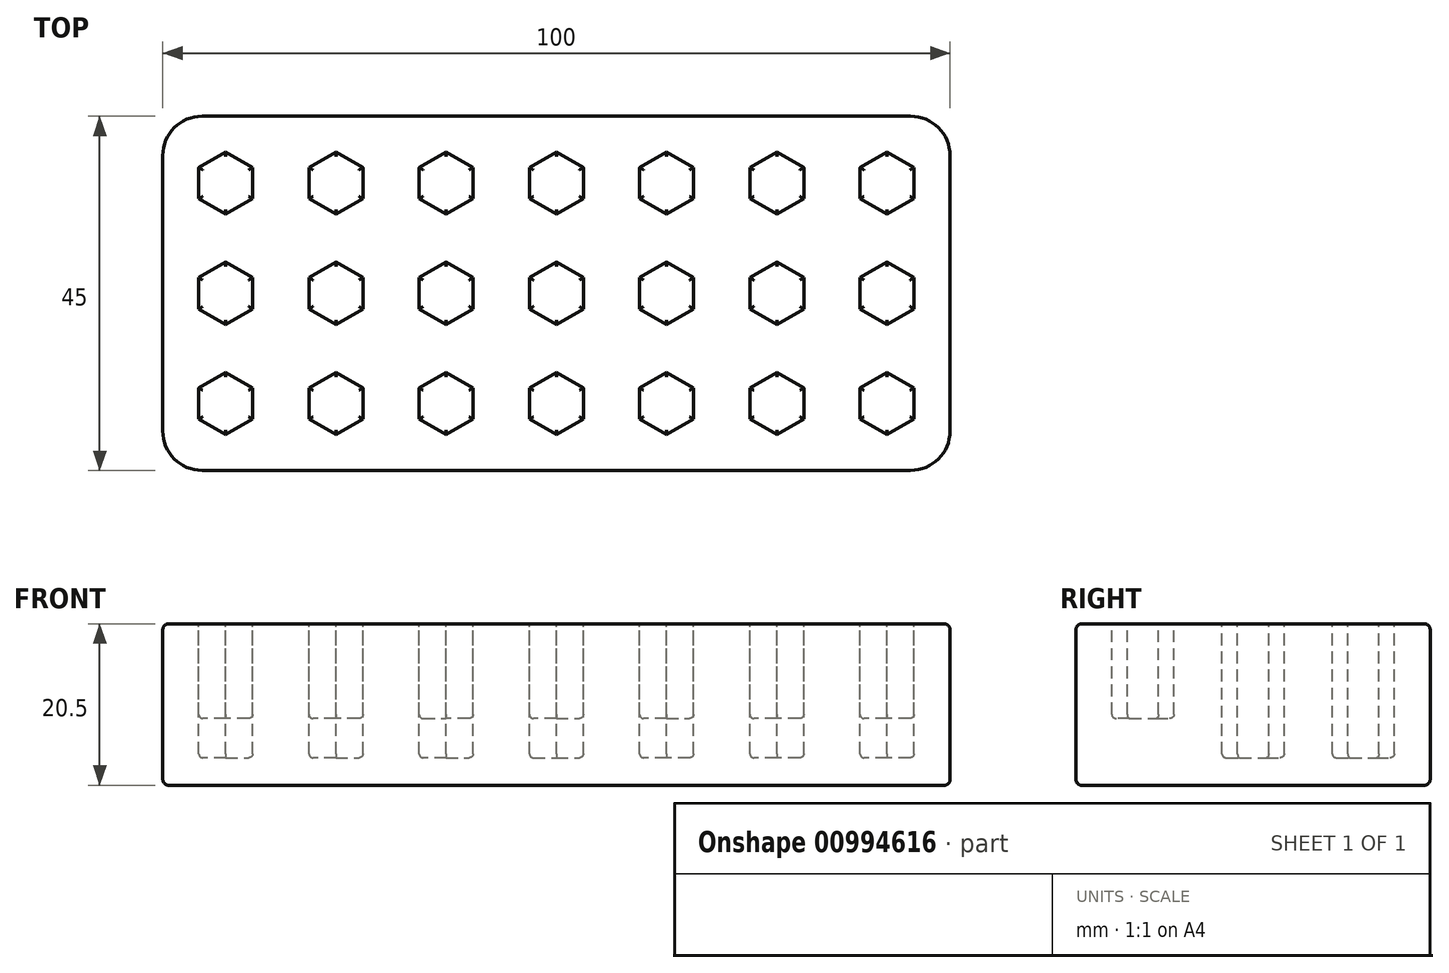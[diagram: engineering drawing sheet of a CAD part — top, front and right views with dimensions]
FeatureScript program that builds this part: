
annotation { "Feature Type Name" : "Feature", "Feature Type Description" : "" }
export const myFeature = defineFeature(function(context is Context, id is Id, definition is map)
    precondition{}
    {
        {
            var Q0;
            Q0=qCreatedBy(makeId("Top.planeOp"),FACE);
            var sketch = newSketch(context, id + "F0", { "sketchPlane" : qUnion([Q0])});
            skLineSegment(sketch, "E0.bottom", {"start": v(45, -22.5) * mm, "end": v(-45, -22.5) * mm});
            skLineSegment(sketch, "E0.top", {"start": v(45, 22.5) * mm, "end": v(-45, 22.5) * mm});
            skLineSegment(sketch, "E0.left", {"start": v(50, -17.5) * mm, "end": v(50, 17.5) * mm});
            skLineSegment(sketch, "E0.right", {"start": v(-50, -17.5) * mm, "end": v(-50, 17.5) * mm});
            skPoint(sketch, "E0.middle", {"position": v(0, 0) * mm});
            skPoint(sketch, "E1.visualSharp", {"position": v(-50, 22.5) * mm});
            skArc(sketch, "E1.filletArc", {"start": v(-45, 22.5) * mm, "mid": v(-48.54, 21.04) * mm, "end": v(-50, 17.5) * mm});
            skPoint(sketch, "E2.visualSharp", {"position": v(50, 22.5) * mm});
            skArc(sketch, "E2.filletArc", {"start": v(50, 17.5) * mm, "mid": v(48.54, 21.04) * mm, "end": v(45, 22.5) * mm});
            skPoint(sketch, "E3.visualSharp", {"position": v(50, -22.5) * mm});
            skArc(sketch, "E3.filletArc", {"start": v(45, -22.5) * mm, "mid": v(48.54, -21.04) * mm, "end": v(50, -17.5) * mm});
            skPoint(sketch, "E4.visualSharp", {"position": v(-50, -22.5) * mm});
            skArc(sketch, "E4.filletArc", {"start": v(-50, -17.5) * mm, "mid": v(-48.54, -21.04) * mm, "end": v(-45, -22.5) * mm});
            skCircle(sketch, "E5.cCircle", {"center": v(0, 0) * mm, "radius": 3.43 * mm, "construction": true});
            skLineSegment(sketch, "E5.0", {"start": v(3.43, 1.98) * mm, "end": v(3.43, -1.98) * mm});
            skLineSegment(sketch, "E5.1", {"start": v(3.43, -1.98) * mm, "end": v(0, -3.95) * mm});
            skLineSegment(sketch, "E5.2", {"start": v(0, -3.95) * mm, "end": v(-3.43, -1.98) * mm});
            skLineSegment(sketch, "E5.3", {"start": v(-3.43, -1.98) * mm, "end": v(-3.43, 1.98) * mm});
            skLineSegment(sketch, "E5.4", {"start": v(-3.43, 1.98) * mm, "end": v(0, 3.95) * mm});
            skLineSegment(sketch, "E5.5", {"start": v(0, 3.95) * mm, "end": v(3.43, 1.98) * mm});
            skPoint(sketch, "E5.0.midPoint", {"position": v(3.43, 0) * mm});
            skLineSegment(sketch, "E6.0.1.0", {"start": v(-3.43, 15.98) * mm, "end": v(0, 17.95) * mm});
            skLineSegment(sketch, "E6.0.1.1", {"start": v(3.43, 12.02) * mm, "end": v(0, 10.05) * mm});
            skLineSegment(sketch, "E6.0.1.2", {"start": v(3.43, 15.98) * mm, "end": v(3.43, 12.02) * mm});
            skPoint(sketch, "E6.0.1.3", {"position": v(3.43, 14) * mm});
            skLineSegment(sketch, "E6.0.1.4", {"start": v(0, 10.05) * mm, "end": v(-3.43, 12.02) * mm});
            skLineSegment(sketch, "E6.0.1.5", {"start": v(-3.43, 12.02) * mm, "end": v(-3.43, 15.98) * mm});
            skCircle(sketch, "E6.0.1.6", {"center": v(0, 14) * mm, "radius": 3.43 * mm, "construction": true});
            skLineSegment(sketch, "E6.0.1.7", {"start": v(0, 17.95) * mm, "end": v(3.43, 15.98) * mm});
            skPoint(sketch, "E6.0.1.8", {"position": v(0, 14) * mm});
            skLineSegment(sketch, "E6.1.0.0", {"start": v(10.58, 1.98) * mm, "end": v(14, 3.95) * mm});
            skLineSegment(sketch, "E6.1.0.1", {"start": v(17.43, -1.98) * mm, "end": v(14, -3.95) * mm});
            skLineSegment(sketch, "E6.1.0.2", {"start": v(17.43, 1.98) * mm, "end": v(17.43, -1.98) * mm});
            skPoint(sketch, "E6.1.0.3", {"position": v(17.43, 0) * mm});
            skLineSegment(sketch, "E6.1.0.4", {"start": v(14, -3.95) * mm, "end": v(10.58, -1.98) * mm});
            skLineSegment(sketch, "E6.1.0.5", {"start": v(10.58, -1.98) * mm, "end": v(10.58, 1.98) * mm});
            skCircle(sketch, "E6.1.0.6", {"center": v(14, 0) * mm, "radius": 3.43 * mm, "construction": true});
            skLineSegment(sketch, "E6.1.0.7", {"start": v(14, 3.95) * mm, "end": v(17.43, 1.98) * mm});
            skPoint(sketch, "E6.1.0.8", {"position": v(14, 0) * mm});
            skLineSegment(sketch, "E6.1.1.0", {"start": v(10.58, 15.98) * mm, "end": v(14, 17.95) * mm});
            skLineSegment(sketch, "E6.1.1.1", {"start": v(17.43, 12.02) * mm, "end": v(14, 10.05) * mm});
            skLineSegment(sketch, "E6.1.1.2", {"start": v(17.43, 15.98) * mm, "end": v(17.43, 12.02) * mm});
            skPoint(sketch, "E6.1.1.3", {"position": v(17.43, 14) * mm});
            skLineSegment(sketch, "E6.1.1.4", {"start": v(14, 10.05) * mm, "end": v(10.58, 12.02) * mm});
            skLineSegment(sketch, "E6.1.1.5", {"start": v(10.58, 12.02) * mm, "end": v(10.58, 15.98) * mm});
            skCircle(sketch, "E6.1.1.6", {"center": v(14, 14) * mm, "radius": 3.43 * mm, "construction": true});
            skLineSegment(sketch, "E6.1.1.7", {"start": v(14, 17.95) * mm, "end": v(17.43, 15.98) * mm});
            skPoint(sketch, "E6.1.1.8", {"position": v(14, 14) * mm});
            skLineSegment(sketch, "E6.2.0.0", {"start": v(24.58, 1.98) * mm, "end": v(28, 3.95) * mm});
            skLineSegment(sketch, "E6.2.0.1", {"start": v(31.43, -1.98) * mm, "end": v(28, -3.95) * mm});
            skLineSegment(sketch, "E6.2.0.2", {"start": v(31.43, 1.98) * mm, "end": v(31.43, -1.98) * mm});
            skPoint(sketch, "E6.2.0.3", {"position": v(31.43, 0) * mm});
            skLineSegment(sketch, "E6.2.0.4", {"start": v(28, -3.95) * mm, "end": v(24.58, -1.98) * mm});
            skLineSegment(sketch, "E6.2.0.5", {"start": v(24.58, -1.98) * mm, "end": v(24.58, 1.98) * mm});
            skCircle(sketch, "E6.2.0.6", {"center": v(28, 0) * mm, "radius": 3.43 * mm, "construction": true});
            skLineSegment(sketch, "E6.2.0.7", {"start": v(28, 3.95) * mm, "end": v(31.43, 1.98) * mm});
            skPoint(sketch, "E6.2.0.8", {"position": v(28, 0) * mm});
            skLineSegment(sketch, "E6.2.1.0", {"start": v(24.58, 15.98) * mm, "end": v(28, 17.95) * mm});
            skLineSegment(sketch, "E6.2.1.1", {"start": v(31.43, 12.02) * mm, "end": v(28, 10.05) * mm});
            skLineSegment(sketch, "E6.2.1.2", {"start": v(31.43, 15.98) * mm, "end": v(31.43, 12.02) * mm});
            skPoint(sketch, "E6.2.1.3", {"position": v(31.43, 14) * mm});
            skLineSegment(sketch, "E6.2.1.4", {"start": v(28, 10.05) * mm, "end": v(24.58, 12.02) * mm});
            skLineSegment(sketch, "E6.2.1.5", {"start": v(24.58, 12.02) * mm, "end": v(24.58, 15.98) * mm});
            skCircle(sketch, "E6.2.1.6", {"center": v(28, 14) * mm, "radius": 3.43 * mm, "construction": true});
            skLineSegment(sketch, "E6.2.1.7", {"start": v(28, 17.95) * mm, "end": v(31.43, 15.98) * mm});
            skPoint(sketch, "E6.2.1.8", {"position": v(28, 14) * mm});
            skLineSegment(sketch, "E6.3.0.0", {"start": v(38.58, 1.98) * mm, "end": v(42, 3.95) * mm});
            skLineSegment(sketch, "E6.3.0.1", {"start": v(45.43, -1.98) * mm, "end": v(42, -3.95) * mm});
            skLineSegment(sketch, "E6.3.0.2", {"start": v(45.43, 1.98) * mm, "end": v(45.43, -1.98) * mm});
            skPoint(sketch, "E6.3.0.3", {"position": v(45.43, 0) * mm});
            skLineSegment(sketch, "E6.3.0.4", {"start": v(42, -3.95) * mm, "end": v(38.58, -1.98) * mm});
            skLineSegment(sketch, "E6.3.0.5", {"start": v(38.58, -1.98) * mm, "end": v(38.58, 1.98) * mm});
            skCircle(sketch, "E6.3.0.6", {"center": v(42, 0) * mm, "radius": 3.43 * mm, "construction": true});
            skLineSegment(sketch, "E6.3.0.7", {"start": v(42, 3.95) * mm, "end": v(45.43, 1.98) * mm});
            skPoint(sketch, "E6.3.0.8", {"position": v(42, 0) * mm});
            skLineSegment(sketch, "E6.3.1.0", {"start": v(38.58, 15.98) * mm, "end": v(42, 17.95) * mm});
            skLineSegment(sketch, "E6.3.1.1", {"start": v(45.43, 12.02) * mm, "end": v(42, 10.05) * mm});
            skLineSegment(sketch, "E6.3.1.2", {"start": v(45.43, 15.98) * mm, "end": v(45.43, 12.02) * mm});
            skPoint(sketch, "E6.3.1.3", {"position": v(45.43, 14) * mm});
            skLineSegment(sketch, "E6.3.1.4", {"start": v(42, 10.05) * mm, "end": v(38.58, 12.02) * mm});
            skLineSegment(sketch, "E6.3.1.5", {"start": v(38.58, 12.02) * mm, "end": v(38.58, 15.98) * mm});
            skCircle(sketch, "E6.3.1.6", {"center": v(42, 14) * mm, "radius": 3.43 * mm, "construction": true});
            skLineSegment(sketch, "E6.3.1.7", {"start": v(42, 17.95) * mm, "end": v(45.43, 15.98) * mm});
            skPoint(sketch, "E6.3.1.8", {"position": v(42, 14) * mm});
            skLineSegment(sketch, "E6.direction1", {"start": v(-3.43, -1.98) * mm, "end": v(10.58, -1.98) * mm, "construction": true});
            skLineSegment(sketch, "E6.direction2", {"start": v(-3.43, -1.98) * mm, "end": v(-3.43, 12.02) * mm, "construction": true});
            skLineSegment(sketch, "E7", {"start": v(0, 36.48) * mm, "end": v(0, -38.23) * mm, "construction": true});
            skLineSegment(sketch, "E8.MirrorCS", {"start": v(-10.58, 15.98) * mm, "end": v(-14, 17.95) * mm});
            skLineSegment(sketch, "E9.MirrorCS", {"start": v(-14, 17.95) * mm, "end": v(-17.43, 15.98) * mm});
            skLineSegment(sketch, "E10.MirrorCS", {"start": v(-17.43, 15.98) * mm, "end": v(-17.43, 12.02) * mm});
            skLineSegment(sketch, "E11.MirrorCS", {"start": v(-17.43, 12.02) * mm, "end": v(-14, 10.05) * mm});
            skLineSegment(sketch, "E12.MirrorCS", {"start": v(-14, 10.05) * mm, "end": v(-10.58, 12.02) * mm});
            skLineSegment(sketch, "E13.MirrorCS", {"start": v(-10.58, 12.02) * mm, "end": v(-10.58, 15.98) * mm});
            skLineSegment(sketch, "E14.MirrorCS", {"start": v(-24.58, 12.02) * mm, "end": v(-24.58, 15.98) * mm});
            skLineSegment(sketch, "E15.MirrorCS", {"start": v(-24.58, 15.98) * mm, "end": v(-28, 17.95) * mm});
            skLineSegment(sketch, "E16.MirrorCS", {"start": v(-28, 17.95) * mm, "end": v(-31.43, 15.98) * mm});
            skLineSegment(sketch, "E17.MirrorCS", {"start": v(-31.43, 15.98) * mm, "end": v(-31.43, 12.02) * mm});
            skLineSegment(sketch, "E18.MirrorCS", {"start": v(-31.43, 12.02) * mm, "end": v(-28, 10.05) * mm});
            skLineSegment(sketch, "E19.MirrorCS", {"start": v(-28, 3.95) * mm, "end": v(-31.43, 1.98) * mm});
            skLineSegment(sketch, "E20.MirrorCS", {"start": v(-24.58, 1.98) * mm, "end": v(-28, 3.95) * mm});
            skLineSegment(sketch, "E21.MirrorCS", {"start": v(-24.58, -1.98) * mm, "end": v(-24.58, 1.98) * mm});
            skLineSegment(sketch, "E22.MirrorCS", {"start": v(-28, -3.95) * mm, "end": v(-24.58, -1.98) * mm});
            skLineSegment(sketch, "E23.MirrorCS", {"start": v(-31.43, -1.98) * mm, "end": v(-28, -3.95) * mm});
            skLineSegment(sketch, "E24.MirrorCS", {"start": v(-28, 10.05) * mm, "end": v(-24.58, 12.02) * mm});
            skLineSegment(sketch, "E25.MirrorCS", {"start": v(-31.43, 1.98) * mm, "end": v(-31.43, -1.98) * mm});
            skLineSegment(sketch, "E26.MirrorCS", {"start": v(-38.58, 15.98) * mm, "end": v(-42, 17.95) * mm});
            skLineSegment(sketch, "E27.MirrorCS", {"start": v(-42, 17.95) * mm, "end": v(-45.43, 15.98) * mm});
            skLineSegment(sketch, "E28.MirrorCS", {"start": v(-45.43, 15.98) * mm, "end": v(-45.43, 12.02) * mm});
            skLineSegment(sketch, "E29.MirrorCS", {"start": v(-45.43, 12.02) * mm, "end": v(-42, 10.05) * mm});
            skLineSegment(sketch, "E30.MirrorCS", {"start": v(-42, 10.05) * mm, "end": v(-38.58, 12.02) * mm});
            skLineSegment(sketch, "E31.MirrorCS", {"start": v(-38.58, 12.02) * mm, "end": v(-38.58, 15.98) * mm});
            skLineSegment(sketch, "E32.MirrorCS", {"start": v(-38.58, 1.98) * mm, "end": v(-42, 3.95) * mm});
            skLineSegment(sketch, "E33.MirrorCS", {"start": v(-42, 3.95) * mm, "end": v(-45.43, 1.98) * mm});
            skLineSegment(sketch, "E34.MirrorCS", {"start": v(-45.43, 1.98) * mm, "end": v(-45.43, -1.98) * mm});
            skLineSegment(sketch, "E35.MirrorCS", {"start": v(-45.43, -1.98) * mm, "end": v(-42, -3.95) * mm});
            skLineSegment(sketch, "E36.MirrorCS", {"start": v(-42, -3.95) * mm, "end": v(-38.58, -1.98) * mm});
            skLineSegment(sketch, "E37.MirrorCS", {"start": v(-38.58, -1.98) * mm, "end": v(-38.58, 1.98) * mm});
            skLineSegment(sketch, "E38.MirrorCS", {"start": v(-10.58, 1.98) * mm, "end": v(-14, 3.95) * mm});
            skLineSegment(sketch, "E39.MirrorCS", {"start": v(-14, 3.95) * mm, "end": v(-17.43, 1.98) * mm});
            skLineSegment(sketch, "E40.MirrorCS", {"start": v(-17.43, 1.98) * mm, "end": v(-17.43, -1.98) * mm});
            skLineSegment(sketch, "E41.MirrorCS", {"start": v(-17.43, -1.98) * mm, "end": v(-14, -3.95) * mm});
            skLineSegment(sketch, "E42.MirrorCS", {"start": v(-14, -3.95) * mm, "end": v(-10.58, -1.98) * mm});
            skLineSegment(sketch, "E43.MirrorCS", {"start": v(-10.58, -1.98) * mm, "end": v(-10.58, 1.98) * mm});
            skLineSegment(sketch, "E44", {"start": v(-62.75, 0) * mm, "end": v(58.2, 0) * mm, "construction": true});
            skLineSegment(sketch, "E45.MirrorCS", {"start": v(-31.43, -12.02) * mm, "end": v(-28, -10.05) * mm});
            skLineSegment(sketch, "E46.MirrorCS", {"start": v(-45.43, -12.02) * mm, "end": v(-42, -10.05) * mm});
            skLineSegment(sketch, "E47.MirrorCS", {"start": v(-28, -17.95) * mm, "end": v(-31.43, -15.98) * mm});
            skLineSegment(sketch, "E48.MirrorCS", {"start": v(-10.58, -15.98) * mm, "end": v(-14, -17.95) * mm});
            skLineSegment(sketch, "E49.MirrorCS", {"start": v(-38.58, -12.02) * mm, "end": v(-38.58, -15.98) * mm});
            skLineSegment(sketch, "E50.MirrorCS", {"start": v(-42, -10.05) * mm, "end": v(-38.58, -12.02) * mm});
            skLineSegment(sketch, "E51.MirrorCS", {"start": v(-31.43, -15.98) * mm, "end": v(-31.43, -12.02) * mm});
            skLineSegment(sketch, "E52.MirrorCS", {"start": v(-45.43, -15.98) * mm, "end": v(-45.43, -12.02) * mm});
            skLineSegment(sketch, "E53.MirrorCS", {"start": v(-24.58, -15.98) * mm, "end": v(-28, -17.95) * mm});
            skLineSegment(sketch, "E54.MirrorCS", {"start": v(-38.58, -15.98) * mm, "end": v(-42, -17.95) * mm});
            skLineSegment(sketch, "E55.MirrorCS", {"start": v(-14, -10.05) * mm, "end": v(-10.58, -12.02) * mm});
            skLineSegment(sketch, "E56.MirrorCS", {"start": v(-10.58, -12.02) * mm, "end": v(-10.58, -15.98) * mm});
            skLineSegment(sketch, "E57.MirrorCS", {"start": v(-28, -10.05) * mm, "end": v(-24.58, -12.02) * mm});
            skLineSegment(sketch, "E58.MirrorCS", {"start": v(-17.43, -12.02) * mm, "end": v(-14, -10.05) * mm});
            skLineSegment(sketch, "E59.MirrorCS", {"start": v(-17.43, -15.98) * mm, "end": v(-17.43, -12.02) * mm});
            skLineSegment(sketch, "E60.MirrorCS", {"start": v(-14, -17.95) * mm, "end": v(-17.43, -15.98) * mm});
            skLineSegment(sketch, "E61.MirrorCS", {"start": v(-42, -17.95) * mm, "end": v(-45.43, -15.98) * mm});
            skLineSegment(sketch, "E62.MirrorCS", {"start": v(-24.58, -12.02) * mm, "end": v(-24.58, -15.98) * mm});
            skLineSegment(sketch, "E63.MirrorCS", {"start": v(-3.43, -15.98) * mm, "end": v(0, -17.95) * mm});
            skLineSegment(sketch, "E64.MirrorCS", {"start": v(0, -17.95) * mm, "end": v(3.43, -15.98) * mm});
            skLineSegment(sketch, "E65.MirrorCS", {"start": v(3.43, -15.98) * mm, "end": v(3.43, -12.02) * mm});
            skLineSegment(sketch, "E66.MirrorCS", {"start": v(3.43, -12.02) * mm, "end": v(0, -10.05) * mm});
            skLineSegment(sketch, "E67.MirrorCS", {"start": v(0, -10.05) * mm, "end": v(-3.43, -12.02) * mm});
            skLineSegment(sketch, "E68.MirrorCS", {"start": v(-3.43, -12.02) * mm, "end": v(-3.43, -15.98) * mm});
            skLineSegment(sketch, "E69.MirrorCS", {"start": v(10.58, -15.98) * mm, "end": v(14, -17.95) * mm});
            skLineSegment(sketch, "E70.MirrorCS", {"start": v(14, -17.95) * mm, "end": v(17.43, -15.98) * mm});
            skLineSegment(sketch, "E71.MirrorCS", {"start": v(17.43, -15.98) * mm, "end": v(17.43, -12.02) * mm});
            skLineSegment(sketch, "E72.MirrorCS", {"start": v(17.43, -12.02) * mm, "end": v(14, -10.05) * mm});
            skLineSegment(sketch, "E73.MirrorCS", {"start": v(14, -10.05) * mm, "end": v(10.58, -12.02) * mm});
            skLineSegment(sketch, "E74.MirrorCS", {"start": v(10.58, -12.02) * mm, "end": v(10.58, -15.98) * mm});
            skLineSegment(sketch, "E75.MirrorCS", {"start": v(28, -10.05) * mm, "end": v(24.58, -12.02) * mm});
            skLineSegment(sketch, "E76.MirrorCS", {"start": v(24.58, -12.02) * mm, "end": v(24.58, -15.98) * mm});
            skLineSegment(sketch, "E77.MirrorCS", {"start": v(24.58, -15.98) * mm, "end": v(28, -17.95) * mm});
            skLineSegment(sketch, "E78.MirrorCS", {"start": v(28, -17.95) * mm, "end": v(31.43, -15.98) * mm});
            skLineSegment(sketch, "E79.MirrorCS", {"start": v(31.43, -15.98) * mm, "end": v(31.43, -12.02) * mm});
            skLineSegment(sketch, "E80.MirrorCS", {"start": v(31.43, -12.02) * mm, "end": v(28, -10.05) * mm});
            skLineSegment(sketch, "E81.MirrorCS", {"start": v(42, -10.05) * mm, "end": v(38.58, -12.02) * mm});
            skLineSegment(sketch, "E82.MirrorCS", {"start": v(38.58, -12.02) * mm, "end": v(38.58, -15.98) * mm});
            skLineSegment(sketch, "E83.MirrorCS", {"start": v(38.58, -15.98) * mm, "end": v(42, -17.95) * mm});
            skLineSegment(sketch, "E84.MirrorCS", {"start": v(42, -17.95) * mm, "end": v(45.43, -15.98) * mm});
            skLineSegment(sketch, "E85.MirrorCS", {"start": v(45.43, -15.98) * mm, "end": v(45.43, -12.02) * mm});
            skLineSegment(sketch, "E86.MirrorCS", {"start": v(45.43, -12.02) * mm, "end": v(42, -10.05) * mm});
            skSolve(sketch);
        }
        {
            var Q0;
            Q0=qCreatedBy(makeId("Top.planeOp"),FACE);
            var sketch = newSketch(context, id + "F1", { "sketchPlane" : qUnion([Q0])});
            skArc(sketch, "E87.0", {"start": v(-45, 22.5) * mm, "mid": v(-48.54, 21.04) * mm, "end": v(-50, 17.5) * mm});
            skLineSegment(sketch, "E88.0", {"start": v(45, 22.5) * mm, "end": v(-45, 22.5) * mm});
            skArc(sketch, "E89.0", {"start": v(50, 17.5) * mm, "mid": v(48.54, 21.04) * mm, "end": v(45, 22.5) * mm});
            skLineSegment(sketch, "E90.0", {"start": v(50, -17.5) * mm, "end": v(50, 17.5) * mm});
            skArc(sketch, "E91.0", {"start": v(45, -22.5) * mm, "mid": v(48.54, -21.04) * mm, "end": v(50, -17.5) * mm});
            skLineSegment(sketch, "E92.0", {"start": v(45, -22.5) * mm, "end": v(-45, -22.5) * mm});
            skArc(sketch, "E93.0", {"start": v(-50, -17.5) * mm, "mid": v(-48.54, -21.04) * mm, "end": v(-45, -22.5) * mm});
            skLineSegment(sketch, "E94.0", {"start": v(-50, -17.5) * mm, "end": v(-50, 17.5) * mm});
            skSolve(sketch);
        }
        {
            var Q0;
            Q0=qSketchRegion(id+"F1",true);
            extrude(context, id + "F2", {"entities" : qUnion([Q0]), "oppositeDirection" : true, "depth" : 20.5 * mm, "offsetDistance" : 25 * mm});
        }
        {
            var Q0;
            Q0=makeQuery(id+"F0.imprint","IMPRINT",FACE,{"disambiguationData":[TD([[makeQuery(id+"F0.imprint","IMPRINT",EDGE,{"derivedFrom":sQuery(id+"F0.wireOp",EDGE,"E46.MirrorCS")}),-1.0]])]});
            var Q1;
            Q1=makeQuery(id+"F0.imprint","IMPRINT",FACE,{"disambiguationData":[TD([[makeQuery(id+"F0.imprint","IMPRINT",EDGE,{"derivedFrom":sQuery(id+"F0.wireOp",EDGE,"E47.MirrorCS")}),-1.0]])]});
            var Q2;
            Q2=makeQuery(id+"F0.imprint","IMPRINT",FACE,{"disambiguationData":[TD([[makeQuery(id+"F0.imprint","IMPRINT",EDGE,{"derivedFrom":sQuery(id+"F0.wireOp",EDGE,"E48.MirrorCS")}),-1.0]])]});
            var Q3;
            Q3=makeQuery(id+"F0.imprint","IMPRINT",FACE,{"disambiguationData":[TD([[makeQuery(id+"F0.imprint","IMPRINT",EDGE,{"derivedFrom":sQuery(id+"F0.wireOp",EDGE,"E63.MirrorCS")}),1.0]])]});
            var Q4;
            Q4=makeQuery(id+"F0.imprint","IMPRINT",FACE,{"disambiguationData":[TD([[makeQuery(id+"F0.imprint","IMPRINT",EDGE,{"derivedFrom":sQuery(id+"F0.wireOp",EDGE,"E69.MirrorCS")}),1.0]])]});
            var Q5;
            Q5=makeQuery(id+"F0.imprint","IMPRINT",FACE,{"disambiguationData":[TD([[makeQuery(id+"F0.imprint","IMPRINT",EDGE,{"derivedFrom":sQuery(id+"F0.wireOp",EDGE,"E75.MirrorCS")}),1.0]])]});
            var Q6;
            Q6=makeQuery(id+"F0.imprint","IMPRINT",FACE,{"disambiguationData":[TD([[makeQuery(id+"F0.imprint","IMPRINT",EDGE,{"derivedFrom":sQuery(id+"F0.wireOp",EDGE,"E81.MirrorCS")}),1.0]])]});
            extrude(context, id + "F3", {"entities" : qUnion([Q0, Q1, Q2, Q3, Q4, Q5, Q6]), "operationType" : NewBodyOperationType.REMOVE, "oppositeDirection" : true, "depth" : 12 * mm, "offsetDistance" : 25 * mm});
        }
        {
            var Q0;
            Q0=makeQuery(id+"F0.imprint","IMPRINT",FACE,{"disambiguationData":[TD([[makeQuery(id+"F0.imprint","IMPRINT",EDGE,{"derivedFrom":sQuery(id+"F0.wireOp",EDGE,"E26.MirrorCS")}),1.0]])]});
            var Q1;
            Q1=makeQuery(id+"F0.imprint","IMPRINT",FACE,{"disambiguationData":[TD([[makeQuery(id+"F0.imprint","IMPRINT",EDGE,{"derivedFrom":sQuery(id+"F0.wireOp",EDGE,"E14.MirrorCS")}),1.0]])]});
            var Q2;
            Q2=makeQuery(id+"F0.imprint","IMPRINT",FACE,{"disambiguationData":[TD([[makeQuery(id+"F0.imprint","IMPRINT",EDGE,{"derivedFrom":sQuery(id+"F0.wireOp",EDGE,"E8.MirrorCS")}),1.0]])]});
            var Q3;
            Q3=makeQuery(id+"F0.imprint","IMPRINT",FACE,{"disambiguationData":[TD([[makeQuery(id+"F0.imprint","IMPRINT",EDGE,{"derivedFrom":sQuery(id+"F0.wireOp",EDGE,"E6.0.1.0")}),-1.0]])]});
            var Q4;
            Q4=makeQuery(id+"F0.imprint","IMPRINT",FACE,{"disambiguationData":[TD([[makeQuery(id+"F0.imprint","IMPRINT",EDGE,{"derivedFrom":sQuery(id+"F0.wireOp",EDGE,"E6.1.1.0")}),-1.0]])]});
            var Q5;
            Q5=makeQuery(id+"F0.imprint","IMPRINT",FACE,{"disambiguationData":[TD([[makeQuery(id+"F0.imprint","IMPRINT",EDGE,{"derivedFrom":sQuery(id+"F0.wireOp",EDGE,"E6.2.1.0")}),-1.0]])]});
            var Q6;
            Q6=makeQuery(id+"F0.imprint","IMPRINT",FACE,{"disambiguationData":[TD([[makeQuery(id+"F0.imprint","IMPRINT",EDGE,{"derivedFrom":sQuery(id+"F0.wireOp",EDGE,"E6.3.1.0")}),-1.0]])]});
            var Q7;
            Q7=makeQuery(id+"F0.imprint","IMPRINT",FACE,{"disambiguationData":[TD([[makeQuery(id+"F0.imprint","IMPRINT",EDGE,{"derivedFrom":sQuery(id+"F0.wireOp",EDGE,"E6.3.0.0")}),-1.0]])]});
            var Q8;
            Q8=makeQuery(id+"F0.imprint","IMPRINT",FACE,{"disambiguationData":[TD([[makeQuery(id+"F0.imprint","IMPRINT",EDGE,{"derivedFrom":sQuery(id+"F0.wireOp",EDGE,"E6.2.0.0")}),-1.0]])]});
            var Q9;
            Q9=makeQuery(id+"F0.imprint","IMPRINT",FACE,{"disambiguationData":[TD([[makeQuery(id+"F0.imprint","IMPRINT",EDGE,{"derivedFrom":sQuery(id+"F0.wireOp",EDGE,"E6.1.0.0")}),-1.0]])]});
            var Q10;
            Q10=makeQuery(id+"F0.imprint","IMPRINT",FACE,{"disambiguationData":[TD([[makeQuery(id+"F0.imprint","IMPRINT",EDGE,{"derivedFrom":sQuery(id+"F0.wireOp",EDGE,"E5.0")}),-1.0]])]});
            var Q11;
            Q11=makeQuery(id+"F0.imprint","IMPRINT",FACE,{"disambiguationData":[TD([[makeQuery(id+"F0.imprint","IMPRINT",EDGE,{"derivedFrom":sQuery(id+"F0.wireOp",EDGE,"E38.MirrorCS")}),1.0]])]});
            var Q12;
            Q12=makeQuery(id+"F0.imprint","IMPRINT",FACE,{"disambiguationData":[TD([[makeQuery(id+"F0.imprint","IMPRINT",EDGE,{"derivedFrom":sQuery(id+"F0.wireOp",EDGE,"E19.MirrorCS")}),1.0]])]});
            var Q13;
            Q13=makeQuery(id+"F0.imprint","IMPRINT",FACE,{"disambiguationData":[TD([[makeQuery(id+"F0.imprint","IMPRINT",EDGE,{"derivedFrom":sQuery(id+"F0.wireOp",EDGE,"E32.MirrorCS")}),1.0]])]});
            extrude(context, id + "F4", {"entities" : qUnion([Q0, Q1, Q2, Q3, Q4, Q5, Q6, Q7, Q8, Q9, Q10, Q11, Q12, Q13]), "operationType" : NewBodyOperationType.REMOVE, "oppositeDirection" : true, "depth" : 17 * mm, "offsetDistance" : 25 * mm});
        }
        {
            var Q0;
            Q0=makeQuery(id+"F4.boolean.opBoolean","COPY",FACE,{"derivedFrom":makeQuery(id+"F4.opExtrude","CAP_FACE",FACE,{"disambiguationData":[OSD([sQuery(id+"F0.wireOp",EDGE,"E26.MirrorCS"),sQuery(id+"F0.wireOp",EDGE,"E27.MirrorCS"),sQuery(id+"F0.wireOp",EDGE,"E28.MirrorCS"),sQuery(id+"F0.wireOp",EDGE,"E29.MirrorCS"),sQuery(id+"F0.wireOp",EDGE,"E30.MirrorCS"),sQuery(id+"F0.wireOp",EDGE,"E31.MirrorCS")])],"isStart":false})});
            var Q1;
            Q1=makeQuery(id+"F4.boolean.opBoolean","COPY",FACE,{"derivedFrom":makeQuery(id+"F4.opExtrude","CAP_FACE",FACE,{"disambiguationData":[OSD([sQuery(id+"F0.wireOp",EDGE,"E14.MirrorCS"),sQuery(id+"F0.wireOp",EDGE,"E15.MirrorCS"),sQuery(id+"F0.wireOp",EDGE,"E16.MirrorCS"),sQuery(id+"F0.wireOp",EDGE,"E17.MirrorCS"),sQuery(id+"F0.wireOp",EDGE,"E18.MirrorCS"),sQuery(id+"F0.wireOp",EDGE,"E24.MirrorCS")])],"isStart":false})});
            var Q2;
            Q2=makeQuery(id+"F4.boolean.opBoolean","COPY",FACE,{"derivedFrom":makeQuery(id+"F4.opExtrude","CAP_FACE",FACE,{"disambiguationData":[OSD([sQuery(id+"F0.wireOp",EDGE,"E8.MirrorCS"),sQuery(id+"F0.wireOp",EDGE,"E9.MirrorCS"),sQuery(id+"F0.wireOp",EDGE,"E10.MirrorCS"),sQuery(id+"F0.wireOp",EDGE,"E11.MirrorCS"),sQuery(id+"F0.wireOp",EDGE,"E12.MirrorCS"),sQuery(id+"F0.wireOp",EDGE,"E13.MirrorCS")])],"isStart":false})});
            var Q3;
            Q3=makeQuery(id+"F4.boolean.opBoolean","COPY",FACE,{"derivedFrom":makeQuery(id+"F4.opExtrude","CAP_FACE",FACE,{"disambiguationData":[OSD([sQuery(id+"F0.wireOp",EDGE,"E6.0.1.0"),sQuery(id+"F0.wireOp",EDGE,"E6.0.1.1"),sQuery(id+"F0.wireOp",EDGE,"E6.0.1.2"),sQuery(id+"F0.wireOp",EDGE,"E6.0.1.4"),sQuery(id+"F0.wireOp",EDGE,"E6.0.1.5"),sQuery(id+"F0.wireOp",EDGE,"E6.0.1.7")])],"isStart":false})});
            var Q4;
            Q4=makeQuery(id+"F4.boolean.opBoolean","COPY",FACE,{"derivedFrom":makeQuery(id+"F4.opExtrude","CAP_FACE",FACE,{"disambiguationData":[OSD([sQuery(id+"F0.wireOp",EDGE,"E6.1.1.0"),sQuery(id+"F0.wireOp",EDGE,"E6.1.1.1"),sQuery(id+"F0.wireOp",EDGE,"E6.1.1.2"),sQuery(id+"F0.wireOp",EDGE,"E6.1.1.4"),sQuery(id+"F0.wireOp",EDGE,"E6.1.1.5"),sQuery(id+"F0.wireOp",EDGE,"E6.1.1.7")])],"isStart":false})});
            var Q5;
            Q5=makeQuery(id+"F4.boolean.opBoolean","COPY",FACE,{"derivedFrom":makeQuery(id+"F4.opExtrude","CAP_FACE",FACE,{"disambiguationData":[OSD([sQuery(id+"F0.wireOp",EDGE,"E6.2.1.0"),sQuery(id+"F0.wireOp",EDGE,"E6.2.1.1"),sQuery(id+"F0.wireOp",EDGE,"E6.2.1.2"),sQuery(id+"F0.wireOp",EDGE,"E6.2.1.4"),sQuery(id+"F0.wireOp",EDGE,"E6.2.1.5"),sQuery(id+"F0.wireOp",EDGE,"E6.2.1.7")])],"isStart":false})});
            var Q6;
            Q6=makeQuery(id+"F4.boolean.opBoolean","COPY",FACE,{"derivedFrom":makeQuery(id+"F4.opExtrude","CAP_FACE",FACE,{"disambiguationData":[OSD([sQuery(id+"F0.wireOp",EDGE,"E6.3.1.0"),sQuery(id+"F0.wireOp",EDGE,"E6.3.1.1"),sQuery(id+"F0.wireOp",EDGE,"E6.3.1.2"),sQuery(id+"F0.wireOp",EDGE,"E6.3.1.4"),sQuery(id+"F0.wireOp",EDGE,"E6.3.1.5"),sQuery(id+"F0.wireOp",EDGE,"E6.3.1.7")])],"isStart":false})});
            var Q7;
            Q7=makeQuery(id+"F4.boolean.opBoolean","COPY",FACE,{"derivedFrom":makeQuery(id+"F4.opExtrude","CAP_FACE",FACE,{"disambiguationData":[OSD([sQuery(id+"F0.wireOp",EDGE,"E6.3.0.0"),sQuery(id+"F0.wireOp",EDGE,"E6.3.0.1"),sQuery(id+"F0.wireOp",EDGE,"E6.3.0.2"),sQuery(id+"F0.wireOp",EDGE,"E6.3.0.4"),sQuery(id+"F0.wireOp",EDGE,"E6.3.0.5"),sQuery(id+"F0.wireOp",EDGE,"E6.3.0.7")])],"isStart":false})});
            var Q8;
            Q8=makeQuery(id+"F4.boolean.opBoolean","COPY",FACE,{"derivedFrom":makeQuery(id+"F4.opExtrude","CAP_FACE",FACE,{"disambiguationData":[OSD([sQuery(id+"F0.wireOp",EDGE,"E6.2.0.0"),sQuery(id+"F0.wireOp",EDGE,"E6.2.0.1"),sQuery(id+"F0.wireOp",EDGE,"E6.2.0.2"),sQuery(id+"F0.wireOp",EDGE,"E6.2.0.4"),sQuery(id+"F0.wireOp",EDGE,"E6.2.0.5"),sQuery(id+"F0.wireOp",EDGE,"E6.2.0.7")])],"isStart":false})});
            var Q9;
            Q9=makeQuery(id+"F4.boolean.opBoolean","COPY",FACE,{"derivedFrom":makeQuery(id+"F4.opExtrude","CAP_FACE",FACE,{"disambiguationData":[OSD([sQuery(id+"F0.wireOp",EDGE,"E6.1.0.0"),sQuery(id+"F0.wireOp",EDGE,"E6.1.0.1"),sQuery(id+"F0.wireOp",EDGE,"E6.1.0.2"),sQuery(id+"F0.wireOp",EDGE,"E6.1.0.4"),sQuery(id+"F0.wireOp",EDGE,"E6.1.0.5"),sQuery(id+"F0.wireOp",EDGE,"E6.1.0.7")])],"isStart":false})});
            var Q10;
            Q10=makeQuery(id+"F4.boolean.opBoolean","COPY",FACE,{"derivedFrom":makeQuery(id+"F4.opExtrude","CAP_FACE",FACE,{"disambiguationData":[OSD([sQuery(id+"F0.wireOp",EDGE,"E5.0"),sQuery(id+"F0.wireOp",EDGE,"E5.1"),sQuery(id+"F0.wireOp",EDGE,"E5.2"),sQuery(id+"F0.wireOp",EDGE,"E5.3"),sQuery(id+"F0.wireOp",EDGE,"E5.4"),sQuery(id+"F0.wireOp",EDGE,"E5.5")])],"isStart":false})});
            var Q11;
            Q11=makeQuery(id+"F4.boolean.opBoolean","COPY",FACE,{"derivedFrom":makeQuery(id+"F4.opExtrude","CAP_FACE",FACE,{"disambiguationData":[OSD([sQuery(id+"F0.wireOp",EDGE,"E38.MirrorCS"),sQuery(id+"F0.wireOp",EDGE,"E39.MirrorCS"),sQuery(id+"F0.wireOp",EDGE,"E40.MirrorCS"),sQuery(id+"F0.wireOp",EDGE,"E41.MirrorCS"),sQuery(id+"F0.wireOp",EDGE,"E42.MirrorCS"),sQuery(id+"F0.wireOp",EDGE,"E43.MirrorCS")])],"isStart":false})});
            var Q12;
            Q12=makeQuery(id+"F4.boolean.opBoolean","COPY",FACE,{"derivedFrom":makeQuery(id+"F4.opExtrude","CAP_FACE",FACE,{"disambiguationData":[OSD([sQuery(id+"F0.wireOp",EDGE,"E19.MirrorCS"),sQuery(id+"F0.wireOp",EDGE,"E20.MirrorCS"),sQuery(id+"F0.wireOp",EDGE,"E22.MirrorCS"),sQuery(id+"F0.wireOp",EDGE,"E23.MirrorCS"),sQuery(id+"F0.wireOp",EDGE,"E21.MirrorCS"),sQuery(id+"F0.wireOp",EDGE,"E25.MirrorCS")])],"isStart":false})});
            var Q13;
            Q13=makeQuery(id+"F4.boolean.opBoolean","COPY",FACE,{"derivedFrom":makeQuery(id+"F4.opExtrude","CAP_FACE",FACE,{"disambiguationData":[OSD([sQuery(id+"F0.wireOp",EDGE,"E32.MirrorCS"),sQuery(id+"F0.wireOp",EDGE,"E33.MirrorCS"),sQuery(id+"F0.wireOp",EDGE,"E34.MirrorCS"),sQuery(id+"F0.wireOp",EDGE,"E35.MirrorCS"),sQuery(id+"F0.wireOp",EDGE,"E36.MirrorCS"),sQuery(id+"F0.wireOp",EDGE,"E37.MirrorCS")])],"isStart":false})});
            var Q14;
            Q14=makeQuery(id+"F3.boolean.opBoolean","COPY",FACE,{"derivedFrom":makeQuery(id+"F3.opExtrude","CAP_FACE",FACE,{"disambiguationData":[OSD([sQuery(id+"F0.wireOp",EDGE,"E46.MirrorCS"),sQuery(id+"F0.wireOp",EDGE,"E49.MirrorCS"),sQuery(id+"F0.wireOp",EDGE,"E50.MirrorCS"),sQuery(id+"F0.wireOp",EDGE,"E52.MirrorCS"),sQuery(id+"F0.wireOp",EDGE,"E54.MirrorCS"),sQuery(id+"F0.wireOp",EDGE,"E61.MirrorCS")])],"isStart":false})});
            var Q15;
            Q15=makeQuery(id+"F3.boolean.opBoolean","COPY",FACE,{"derivedFrom":makeQuery(id+"F3.opExtrude","CAP_FACE",FACE,{"disambiguationData":[OSD([sQuery(id+"F0.wireOp",EDGE,"E47.MirrorCS"),sQuery(id+"F0.wireOp",EDGE,"E51.MirrorCS"),sQuery(id+"F0.wireOp",EDGE,"E45.MirrorCS"),sQuery(id+"F0.wireOp",EDGE,"E53.MirrorCS"),sQuery(id+"F0.wireOp",EDGE,"E57.MirrorCS"),sQuery(id+"F0.wireOp",EDGE,"E62.MirrorCS")])],"isStart":false})});
            var Q16;
            Q16=makeQuery(id+"F3.boolean.opBoolean","COPY",FACE,{"derivedFrom":makeQuery(id+"F3.opExtrude","CAP_FACE",FACE,{"disambiguationData":[OSD([sQuery(id+"F0.wireOp",EDGE,"E48.MirrorCS"),sQuery(id+"F0.wireOp",EDGE,"E55.MirrorCS"),sQuery(id+"F0.wireOp",EDGE,"E56.MirrorCS"),sQuery(id+"F0.wireOp",EDGE,"E58.MirrorCS"),sQuery(id+"F0.wireOp",EDGE,"E59.MirrorCS"),sQuery(id+"F0.wireOp",EDGE,"E60.MirrorCS")])],"isStart":false})});
            var Q17;
            Q17=makeQuery(id+"F3.boolean.opBoolean","COPY",FACE,{"derivedFrom":makeQuery(id+"F3.opExtrude","CAP_FACE",FACE,{"disambiguationData":[OSD([sQuery(id+"F0.wireOp",EDGE,"E63.MirrorCS"),sQuery(id+"F0.wireOp",EDGE,"E64.MirrorCS"),sQuery(id+"F0.wireOp",EDGE,"E65.MirrorCS"),sQuery(id+"F0.wireOp",EDGE,"E66.MirrorCS"),sQuery(id+"F0.wireOp",EDGE,"E67.MirrorCS"),sQuery(id+"F0.wireOp",EDGE,"E68.MirrorCS")])],"isStart":false})});
            var Q18;
            Q18=makeQuery(id+"F3.boolean.opBoolean","COPY",FACE,{"derivedFrom":makeQuery(id+"F3.opExtrude","CAP_FACE",FACE,{"disambiguationData":[OSD([sQuery(id+"F0.wireOp",EDGE,"E69.MirrorCS"),sQuery(id+"F0.wireOp",EDGE,"E70.MirrorCS"),sQuery(id+"F0.wireOp",EDGE,"E71.MirrorCS"),sQuery(id+"F0.wireOp",EDGE,"E72.MirrorCS"),sQuery(id+"F0.wireOp",EDGE,"E73.MirrorCS"),sQuery(id+"F0.wireOp",EDGE,"E74.MirrorCS")])],"isStart":false})});
            var Q19;
            Q19=makeQuery(id+"F3.boolean.opBoolean","COPY",FACE,{"derivedFrom":makeQuery(id+"F3.opExtrude","CAP_FACE",FACE,{"disambiguationData":[OSD([sQuery(id+"F0.wireOp",EDGE,"E75.MirrorCS"),sQuery(id+"F0.wireOp",EDGE,"E76.MirrorCS"),sQuery(id+"F0.wireOp",EDGE,"E77.MirrorCS"),sQuery(id+"F0.wireOp",EDGE,"E78.MirrorCS"),sQuery(id+"F0.wireOp",EDGE,"E79.MirrorCS"),sQuery(id+"F0.wireOp",EDGE,"E80.MirrorCS")])],"isStart":false})});
            var Q20;
            Q20=makeQuery(id+"F3.boolean.opBoolean","COPY",FACE,{"derivedFrom":makeQuery(id+"F3.opExtrude","CAP_FACE",FACE,{"disambiguationData":[OSD([sQuery(id+"F0.wireOp",EDGE,"E81.MirrorCS"),sQuery(id+"F0.wireOp",EDGE,"E82.MirrorCS"),sQuery(id+"F0.wireOp",EDGE,"E83.MirrorCS"),sQuery(id+"F0.wireOp",EDGE,"E84.MirrorCS"),sQuery(id+"F0.wireOp",EDGE,"E85.MirrorCS"),sQuery(id+"F0.wireOp",EDGE,"E86.MirrorCS")])],"isStart":false})});
            fillet(context, id + "F5", {"entities" : qUnion([Q0, Q1, Q2, Q3, Q4, Q5, Q6, Q7, Q8, Q9, Q10, Q11, Q12, Q13, Q14, Q15, Q16, Q17, Q18, Q19, Q20]), "radius" : .5 * mm, "tangentPropagation" : true, "allowEdgeOverflow" : false});
        }
        {
            var Q0;
            Q0=makeQuery(id+"F4.boolean.opBoolean","COPY",EDGE,{"derivedFrom":makeQuery(id+"F4.opExtrude","CAP_EDGE",EDGE,{"disambiguationData":[OSD([sQuery(id+"F0.wireOp",EDGE,"E27.MirrorCS")])],"isStart":true})});
            var Q1;
            Q1=makeQuery(id+"F4.boolean.opBoolean","COPY",EDGE,{"derivedFrom":makeQuery(id+"F4.opExtrude","CAP_EDGE",EDGE,{"disambiguationData":[OSD([sQuery(id+"F0.wireOp",EDGE,"E26.MirrorCS")])],"isStart":true})});
            var Q2;
            Q2=makeQuery(id+"F4.boolean.opBoolean","COPY",EDGE,{"derivedFrom":makeQuery(id+"F4.opExtrude","CAP_EDGE",EDGE,{"disambiguationData":[OSD([sQuery(id+"F0.wireOp",EDGE,"E31.MirrorCS")])],"isStart":true})});
            var Q3;
            Q3=makeQuery(id+"F4.boolean.opBoolean","COPY",EDGE,{"derivedFrom":makeQuery(id+"F4.opExtrude","CAP_EDGE",EDGE,{"disambiguationData":[OSD([sQuery(id+"F0.wireOp",EDGE,"E30.MirrorCS")])],"isStart":true})});
            var Q4;
            Q4=makeQuery(id+"F4.boolean.opBoolean","COPY",EDGE,{"derivedFrom":makeQuery(id+"F4.opExtrude","CAP_EDGE",EDGE,{"disambiguationData":[OSD([sQuery(id+"F0.wireOp",EDGE,"E29.MirrorCS")])],"isStart":true})});
            var Q5;
            Q5=makeQuery(id+"F4.boolean.opBoolean","COPY",EDGE,{"derivedFrom":makeQuery(id+"F4.opExtrude","CAP_EDGE",EDGE,{"disambiguationData":[OSD([sQuery(id+"F0.wireOp",EDGE,"E28.MirrorCS")])],"isStart":true})});
            var Q6;
            Q6=makeQuery(id+"F4.boolean.opBoolean","COPY",EDGE,{"derivedFrom":makeQuery(id+"F4.opExtrude","CAP_EDGE",EDGE,{"disambiguationData":[OSD([sQuery(id+"F0.wireOp",EDGE,"E33.MirrorCS")])],"isStart":true})});
            var Q7;
            Q7=makeQuery(id+"F4.boolean.opBoolean","COPY",EDGE,{"derivedFrom":makeQuery(id+"F4.opExtrude","CAP_EDGE",EDGE,{"disambiguationData":[OSD([sQuery(id+"F0.wireOp",EDGE,"E37.MirrorCS")])],"isStart":true})});
            var Q8;
            Q8=makeQuery(id+"F4.boolean.opBoolean","COPY",EDGE,{"derivedFrom":makeQuery(id+"F4.opExtrude","CAP_EDGE",EDGE,{"disambiguationData":[OSD([sQuery(id+"F0.wireOp",EDGE,"E35.MirrorCS")])],"isStart":true})});
            var Q9;
            Q9=makeQuery(id+"F4.boolean.opBoolean","COPY",EDGE,{"derivedFrom":makeQuery(id+"F4.opExtrude","CAP_EDGE",EDGE,{"disambiguationData":[OSD([sQuery(id+"F0.wireOp",EDGE,"E34.MirrorCS")])],"isStart":true})});
            var Q10;
            Q10=makeQuery(id+"F4.boolean.opBoolean","COPY",EDGE,{"derivedFrom":makeQuery(id+"F4.opExtrude","CAP_EDGE",EDGE,{"disambiguationData":[OSD([sQuery(id+"F0.wireOp",EDGE,"E32.MirrorCS")])],"isStart":true})});
            var Q11;
            Q11=makeQuery(id+"F4.boolean.opBoolean","COPY",EDGE,{"derivedFrom":makeQuery(id+"F4.opExtrude","CAP_EDGE",EDGE,{"disambiguationData":[OSD([sQuery(id+"F0.wireOp",EDGE,"E36.MirrorCS")])],"isStart":true})});
            var Q12;
            Q12=makeQuery(id+"F3.boolean.opBoolean","COPY",EDGE,{"derivedFrom":makeQuery(id+"F3.opExtrude","CAP_EDGE",EDGE,{"disambiguationData":[OSD([sQuery(id+"F0.wireOp",EDGE,"E61.MirrorCS")])],"isStart":true})});
            var Q13;
            Q13=makeQuery(id+"F3.boolean.opBoolean","COPY",EDGE,{"derivedFrom":makeQuery(id+"F3.opExtrude","CAP_EDGE",EDGE,{"disambiguationData":[OSD([sQuery(id+"F0.wireOp",EDGE,"E50.MirrorCS")])],"isStart":true})});
            var Q14;
            Q14=makeQuery(id+"F3.boolean.opBoolean","COPY",EDGE,{"derivedFrom":makeQuery(id+"F3.opExtrude","CAP_EDGE",EDGE,{"disambiguationData":[OSD([sQuery(id+"F0.wireOp",EDGE,"E54.MirrorCS")])],"isStart":true})});
            var Q15;
            Q15=makeQuery(id+"F3.boolean.opBoolean","COPY",EDGE,{"derivedFrom":makeQuery(id+"F3.opExtrude","CAP_EDGE",EDGE,{"disambiguationData":[OSD([sQuery(id+"F0.wireOp",EDGE,"E52.MirrorCS")])],"isStart":true})});
            var Q16;
            Q16=makeQuery(id+"F3.boolean.opBoolean","COPY",EDGE,{"derivedFrom":makeQuery(id+"F3.opExtrude","CAP_EDGE",EDGE,{"disambiguationData":[OSD([sQuery(id+"F0.wireOp",EDGE,"E49.MirrorCS")])],"isStart":true})});
            var Q17;
            Q17=makeQuery(id+"F3.boolean.opBoolean","COPY",EDGE,{"derivedFrom":makeQuery(id+"F3.opExtrude","CAP_EDGE",EDGE,{"disambiguationData":[OSD([sQuery(id+"F0.wireOp",EDGE,"E46.MirrorCS")])],"isStart":true})});
            var Q18;
            Q18=makeQuery(id+"F3.boolean.opBoolean","COPY",EDGE,{"derivedFrom":makeQuery(id+"F3.opExtrude","CAP_EDGE",EDGE,{"disambiguationData":[OSD([sQuery(id+"F0.wireOp",EDGE,"E57.MirrorCS")])],"isStart":true})});
            var Q19;
            Q19=makeQuery(id+"F3.boolean.opBoolean","COPY",EDGE,{"derivedFrom":makeQuery(id+"F3.opExtrude","CAP_EDGE",EDGE,{"disambiguationData":[OSD([sQuery(id+"F0.wireOp",EDGE,"E51.MirrorCS")])],"isStart":true})});
            var Q20;
            Q20=makeQuery(id+"F3.boolean.opBoolean","COPY",EDGE,{"derivedFrom":makeQuery(id+"F3.opExtrude","CAP_EDGE",EDGE,{"disambiguationData":[OSD([sQuery(id+"F0.wireOp",EDGE,"E47.MirrorCS")])],"isStart":true})});
            var Q21;
            Q21=makeQuery(id+"F3.boolean.opBoolean","COPY",EDGE,{"derivedFrom":makeQuery(id+"F3.opExtrude","CAP_EDGE",EDGE,{"disambiguationData":[OSD([sQuery(id+"F0.wireOp",EDGE,"E45.MirrorCS")])],"isStart":true})});
            var Q22;
            Q22=makeQuery(id+"F3.boolean.opBoolean","COPY",EDGE,{"derivedFrom":makeQuery(id+"F3.opExtrude","CAP_EDGE",EDGE,{"disambiguationData":[OSD([sQuery(id+"F0.wireOp",EDGE,"E53.MirrorCS")])],"isStart":true})});
            var Q23;
            Q23=makeQuery(id+"F3.boolean.opBoolean","COPY",EDGE,{"derivedFrom":makeQuery(id+"F3.opExtrude","CAP_EDGE",EDGE,{"disambiguationData":[OSD([sQuery(id+"F0.wireOp",EDGE,"E62.MirrorCS")])],"isStart":true})});
            var Q24;
            Q24=makeQuery(id+"F4.boolean.opBoolean","COPY",EDGE,{"derivedFrom":makeQuery(id+"F4.opExtrude","CAP_EDGE",EDGE,{"disambiguationData":[OSD([sQuery(id+"F0.wireOp",EDGE,"E21.MirrorCS")])],"isStart":true})});
            var Q25;
            Q25=makeQuery(id+"F4.boolean.opBoolean","COPY",EDGE,{"derivedFrom":makeQuery(id+"F4.opExtrude","CAP_EDGE",EDGE,{"disambiguationData":[OSD([sQuery(id+"F0.wireOp",EDGE,"E25.MirrorCS")])],"isStart":true})});
            var Q26;
            Q26=makeQuery(id+"F4.boolean.opBoolean","COPY",EDGE,{"derivedFrom":makeQuery(id+"F4.opExtrude","CAP_EDGE",EDGE,{"disambiguationData":[OSD([sQuery(id+"F0.wireOp",EDGE,"E17.MirrorCS")])],"isStart":true})});
            var Q27;
            Q27=makeQuery(id+"F4.boolean.opBoolean","COPY",EDGE,{"derivedFrom":makeQuery(id+"F4.opExtrude","CAP_EDGE",EDGE,{"disambiguationData":[OSD([sQuery(id+"F0.wireOp",EDGE,"E15.MirrorCS")])],"isStart":true})});
            var Q28;
            Q28=makeQuery(id+"F4.boolean.opBoolean","COPY",EDGE,{"derivedFrom":makeQuery(id+"F4.opExtrude","CAP_EDGE",EDGE,{"disambiguationData":[OSD([sQuery(id+"F0.wireOp",EDGE,"E20.MirrorCS")])],"isStart":true})});
            var Q29;
            Q29=makeQuery(id+"F4.boolean.opBoolean","COPY",EDGE,{"derivedFrom":makeQuery(id+"F4.opExtrude","CAP_EDGE",EDGE,{"disambiguationData":[OSD([sQuery(id+"F0.wireOp",EDGE,"E24.MirrorCS")])],"isStart":true})});
            var Q30;
            Q30=makeQuery(id+"F4.boolean.opBoolean","COPY",EDGE,{"derivedFrom":makeQuery(id+"F4.opExtrude","CAP_EDGE",EDGE,{"disambiguationData":[OSD([sQuery(id+"F0.wireOp",EDGE,"E16.MirrorCS")])],"isStart":true})});
            var Q31;
            Q31=makeQuery(id+"F4.boolean.opBoolean","COPY",EDGE,{"derivedFrom":makeQuery(id+"F4.opExtrude","CAP_EDGE",EDGE,{"disambiguationData":[OSD([sQuery(id+"F0.wireOp",EDGE,"E18.MirrorCS")])],"isStart":true})});
            var Q32;
            Q32=makeQuery(id+"F4.boolean.opBoolean","COPY",EDGE,{"derivedFrom":makeQuery(id+"F4.opExtrude","CAP_EDGE",EDGE,{"disambiguationData":[OSD([sQuery(id+"F0.wireOp",EDGE,"E19.MirrorCS")])],"isStart":true})});
            var Q33;
            Q33=makeQuery(id+"F4.boolean.opBoolean","COPY",EDGE,{"derivedFrom":makeQuery(id+"F4.opExtrude","CAP_EDGE",EDGE,{"disambiguationData":[OSD([sQuery(id+"F0.wireOp",EDGE,"E22.MirrorCS")])],"isStart":true})});
            var Q34;
            Q34=makeQuery(id+"F4.boolean.opBoolean","COPY",EDGE,{"derivedFrom":makeQuery(id+"F4.opExtrude","CAP_EDGE",EDGE,{"disambiguationData":[OSD([sQuery(id+"F0.wireOp",EDGE,"E14.MirrorCS")])],"isStart":true})});
            var Q35;
            Q35=makeQuery(id+"F4.boolean.opBoolean","COPY",EDGE,{"derivedFrom":makeQuery(id+"F4.opExtrude","CAP_EDGE",EDGE,{"disambiguationData":[OSD([sQuery(id+"F0.wireOp",EDGE,"E23.MirrorCS")])],"isStart":true})});
            var Q36;
            Q36=makeQuery(id+"F3.boolean.opBoolean","COPY",EDGE,{"derivedFrom":makeQuery(id+"F3.opExtrude","CAP_EDGE",EDGE,{"disambiguationData":[OSD([sQuery(id+"F0.wireOp",EDGE,"E55.MirrorCS")])],"isStart":true})});
            var Q37;
            Q37=makeQuery(id+"F3.boolean.opBoolean","COPY",EDGE,{"derivedFrom":makeQuery(id+"F3.opExtrude","CAP_EDGE",EDGE,{"disambiguationData":[OSD([sQuery(id+"F0.wireOp",EDGE,"E48.MirrorCS")])],"isStart":true})});
            var Q38;
            Q38=makeQuery(id+"F3.boolean.opBoolean","COPY",EDGE,{"derivedFrom":makeQuery(id+"F3.opExtrude","CAP_EDGE",EDGE,{"disambiguationData":[OSD([sQuery(id+"F0.wireOp",EDGE,"E59.MirrorCS")])],"isStart":true})});
            var Q39;
            Q39=makeQuery(id+"F4.boolean.opBoolean","COPY",EDGE,{"derivedFrom":makeQuery(id+"F4.opExtrude","CAP_EDGE",EDGE,{"disambiguationData":[OSD([sQuery(id+"F0.wireOp",EDGE,"E38.MirrorCS")])],"isStart":true})});
            var Q40;
            Q40=makeQuery(id+"F4.boolean.opBoolean","COPY",EDGE,{"derivedFrom":makeQuery(id+"F4.opExtrude","CAP_EDGE",EDGE,{"disambiguationData":[OSD([sQuery(id+"F0.wireOp",EDGE,"E12.MirrorCS")])],"isStart":true})});
            var Q41;
            Q41=makeQuery(id+"F4.boolean.opBoolean","COPY",EDGE,{"derivedFrom":makeQuery(id+"F4.opExtrude","CAP_EDGE",EDGE,{"disambiguationData":[OSD([sQuery(id+"F0.wireOp",EDGE,"E42.MirrorCS")])],"isStart":true})});
            var Q42;
            Q42=makeQuery(id+"F4.boolean.opBoolean","COPY",EDGE,{"derivedFrom":makeQuery(id+"F4.opExtrude","CAP_EDGE",EDGE,{"disambiguationData":[OSD([sQuery(id+"F0.wireOp",EDGE,"E9.MirrorCS")])],"isStart":true})});
            var Q43;
            Q43=makeQuery(id+"F4.boolean.opBoolean","COPY",EDGE,{"derivedFrom":makeQuery(id+"F4.opExtrude","CAP_EDGE",EDGE,{"disambiguationData":[OSD([sQuery(id+"F0.wireOp",EDGE,"E8.MirrorCS")])],"isStart":true})});
            var Q44;
            Q44=makeQuery(id+"F4.boolean.opBoolean","COPY",EDGE,{"derivedFrom":makeQuery(id+"F4.opExtrude","CAP_EDGE",EDGE,{"disambiguationData":[OSD([sQuery(id+"F0.wireOp",EDGE,"E40.MirrorCS")])],"isStart":true})});
            var Q45;
            Q45=makeQuery(id+"F4.boolean.opBoolean","COPY",EDGE,{"derivedFrom":makeQuery(id+"F4.opExtrude","CAP_EDGE",EDGE,{"disambiguationData":[OSD([sQuery(id+"F0.wireOp",EDGE,"E10.MirrorCS")])],"isStart":true})});
            var Q46;
            Q46=makeQuery(id+"F4.boolean.opBoolean","COPY",EDGE,{"derivedFrom":makeQuery(id+"F4.opExtrude","CAP_EDGE",EDGE,{"disambiguationData":[OSD([sQuery(id+"F0.wireOp",EDGE,"E13.MirrorCS")])],"isStart":true})});
            var Q47;
            Q47=makeQuery(id+"F4.boolean.opBoolean","COPY",EDGE,{"derivedFrom":makeQuery(id+"F4.opExtrude","CAP_EDGE",EDGE,{"disambiguationData":[OSD([sQuery(id+"F0.wireOp",EDGE,"E43.MirrorCS")])],"isStart":true})});
            var Q48;
            Q48=makeQuery(id+"F3.boolean.opBoolean","COPY",EDGE,{"derivedFrom":makeQuery(id+"F3.opExtrude","CAP_EDGE",EDGE,{"disambiguationData":[OSD([sQuery(id+"F0.wireOp",EDGE,"E60.MirrorCS")])],"isStart":true})});
            var Q49;
            Q49=makeQuery(id+"F3.boolean.opBoolean","COPY",EDGE,{"derivedFrom":makeQuery(id+"F3.opExtrude","CAP_EDGE",EDGE,{"disambiguationData":[OSD([sQuery(id+"F0.wireOp",EDGE,"E58.MirrorCS")])],"isStart":true})});
            var Q50;
            Q50=makeQuery(id+"F3.boolean.opBoolean","COPY",EDGE,{"derivedFrom":makeQuery(id+"F3.opExtrude","CAP_EDGE",EDGE,{"disambiguationData":[OSD([sQuery(id+"F0.wireOp",EDGE,"E56.MirrorCS")])],"isStart":true})});
            var Q51;
            Q51=makeQuery(id+"F4.boolean.opBoolean","COPY",EDGE,{"derivedFrom":makeQuery(id+"F4.opExtrude","CAP_EDGE",EDGE,{"disambiguationData":[OSD([sQuery(id+"F0.wireOp",EDGE,"E41.MirrorCS")])],"isStart":true})});
            var Q52;
            Q52=makeQuery(id+"F4.boolean.opBoolean","COPY",EDGE,{"derivedFrom":makeQuery(id+"F4.opExtrude","CAP_EDGE",EDGE,{"disambiguationData":[OSD([sQuery(id+"F0.wireOp",EDGE,"E39.MirrorCS")])],"isStart":true})});
            var Q53;
            Q53=makeQuery(id+"F4.boolean.opBoolean","COPY",EDGE,{"derivedFrom":makeQuery(id+"F4.opExtrude","CAP_EDGE",EDGE,{"disambiguationData":[OSD([sQuery(id+"F0.wireOp",EDGE,"E11.MirrorCS")])],"isStart":true})});
            var Q54;
            Q54=makeQuery(id+"F4.boolean.opBoolean","COPY",EDGE,{"derivedFrom":makeQuery(id+"F4.opExtrude","CAP_EDGE",EDGE,{"disambiguationData":[OSD([sQuery(id+"F0.wireOp",EDGE,"E6.0.1.0")])],"isStart":true})});
            var Q55;
            Q55=makeQuery(id+"F4.boolean.opBoolean","COPY",EDGE,{"derivedFrom":makeQuery(id+"F4.opExtrude","CAP_EDGE",EDGE,{"disambiguationData":[OSD([sQuery(id+"F0.wireOp",EDGE,"E6.0.1.7")])],"isStart":true})});
            var Q56;
            Q56=makeQuery(id+"F4.boolean.opBoolean","COPY",EDGE,{"derivedFrom":makeQuery(id+"F4.opExtrude","CAP_EDGE",EDGE,{"disambiguationData":[OSD([sQuery(id+"F0.wireOp",EDGE,"E6.0.1.5")])],"isStart":true})});
            var Q57;
            Q57=makeQuery(id+"F3.boolean.opBoolean","COPY",EDGE,{"derivedFrom":makeQuery(id+"F3.opExtrude","CAP_EDGE",EDGE,{"disambiguationData":[OSD([sQuery(id+"F0.wireOp",EDGE,"E65.MirrorCS")])],"isStart":true})});
            var Q58;
            Q58=makeQuery(id+"F3.boolean.opBoolean","COPY",EDGE,{"derivedFrom":makeQuery(id+"F3.opExtrude","CAP_EDGE",EDGE,{"disambiguationData":[OSD([sQuery(id+"F0.wireOp",EDGE,"E66.MirrorCS")])],"isStart":true})});
            var Q59;
            Q59=makeQuery(id+"F3.boolean.opBoolean","COPY",EDGE,{"derivedFrom":makeQuery(id+"F3.opExtrude","CAP_EDGE",EDGE,{"disambiguationData":[OSD([sQuery(id+"F0.wireOp",EDGE,"E67.MirrorCS")])],"isStart":true})});
            var Q60;
            Q60=makeQuery(id+"F3.boolean.opBoolean","COPY",EDGE,{"derivedFrom":makeQuery(id+"F3.opExtrude","CAP_EDGE",EDGE,{"disambiguationData":[OSD([sQuery(id+"F0.wireOp",EDGE,"E68.MirrorCS")])],"isStart":true})});
            var Q61;
            Q61=makeQuery(id+"F3.boolean.opBoolean","COPY",EDGE,{"derivedFrom":makeQuery(id+"F3.opExtrude","CAP_EDGE",EDGE,{"disambiguationData":[OSD([sQuery(id+"F0.wireOp",EDGE,"E73.MirrorCS")])],"isStart":true})});
            var Q62;
            Q62=makeQuery(id+"F4.boolean.opBoolean","COPY",EDGE,{"derivedFrom":makeQuery(id+"F4.opExtrude","CAP_EDGE",EDGE,{"disambiguationData":[OSD([sQuery(id+"F0.wireOp",EDGE,"E6.1.1.0")])],"isStart":true})});
            var Q63;
            Q63=makeQuery(id+"F4.boolean.opBoolean","COPY",EDGE,{"derivedFrom":makeQuery(id+"F4.opExtrude","CAP_EDGE",EDGE,{"disambiguationData":[OSD([sQuery(id+"F0.wireOp",EDGE,"E6.1.1.1")])],"isStart":true})});
            var Q64;
            Q64=makeQuery(id+"F4.boolean.opBoolean","COPY",EDGE,{"derivedFrom":makeQuery(id+"F4.opExtrude","CAP_EDGE",EDGE,{"disambiguationData":[OSD([sQuery(id+"F0.wireOp",EDGE,"E5.3")])],"isStart":true})});
            var Q65;
            Q65=makeQuery(id+"F3.boolean.opBoolean","COPY",EDGE,{"derivedFrom":makeQuery(id+"F3.opExtrude","CAP_EDGE",EDGE,{"disambiguationData":[OSD([sQuery(id+"F0.wireOp",EDGE,"E69.MirrorCS")])],"isStart":true})});
            var Q66;
            Q66=makeQuery(id+"F4.boolean.opBoolean","COPY",EDGE,{"derivedFrom":makeQuery(id+"F4.opExtrude","CAP_EDGE",EDGE,{"disambiguationData":[OSD([sQuery(id+"F0.wireOp",EDGE,"E5.1")])],"isStart":true})});
            var Q67;
            Q67=makeQuery(id+"F4.boolean.opBoolean","COPY",EDGE,{"derivedFrom":makeQuery(id+"F4.opExtrude","CAP_EDGE",EDGE,{"disambiguationData":[OSD([sQuery(id+"F0.wireOp",EDGE,"E6.0.1.2")])],"isStart":true})});
            var Q68;
            Q68=makeQuery(id+"F4.boolean.opBoolean","COPY",EDGE,{"derivedFrom":makeQuery(id+"F4.opExtrude","CAP_EDGE",EDGE,{"disambiguationData":[OSD([sQuery(id+"F0.wireOp",EDGE,"E6.1.0.7")])],"isStart":true})});
            var Q69;
            Q69=makeQuery(id+"F4.boolean.opBoolean","COPY",EDGE,{"derivedFrom":makeQuery(id+"F4.opExtrude","CAP_EDGE",EDGE,{"disambiguationData":[OSD([sQuery(id+"F0.wireOp",EDGE,"E6.1.0.2")])],"isStart":true})});
            var Q70;
            Q70=makeQuery(id+"F4.boolean.opBoolean","COPY",EDGE,{"derivedFrom":makeQuery(id+"F4.opExtrude","CAP_EDGE",EDGE,{"disambiguationData":[OSD([sQuery(id+"F0.wireOp",EDGE,"E6.1.1.4")])],"isStart":true})});
            var Q71;
            Q71=makeQuery(id+"F4.boolean.opBoolean","COPY",EDGE,{"derivedFrom":makeQuery(id+"F4.opExtrude","CAP_EDGE",EDGE,{"disambiguationData":[OSD([sQuery(id+"F0.wireOp",EDGE,"E6.1.1.5")])],"isStart":true})});
            var Q72;
            Q72=makeQuery(id+"F4.boolean.opBoolean","COPY",EDGE,{"derivedFrom":makeQuery(id+"F4.opExtrude","CAP_EDGE",EDGE,{"disambiguationData":[OSD([sQuery(id+"F0.wireOp",EDGE,"E6.1.0.0")])],"isStart":true})});
            var Q73;
            Q73=makeQuery(id+"F4.boolean.opBoolean","COPY",EDGE,{"derivedFrom":makeQuery(id+"F4.opExtrude","CAP_EDGE",EDGE,{"disambiguationData":[OSD([sQuery(id+"F0.wireOp",EDGE,"E6.0.1.1")])],"isStart":true})});
            var Q74;
            Q74=makeQuery(id+"F3.boolean.opBoolean","COPY",EDGE,{"derivedFrom":makeQuery(id+"F3.opExtrude","CAP_EDGE",EDGE,{"disambiguationData":[OSD([sQuery(id+"F0.wireOp",EDGE,"E63.MirrorCS")])],"isStart":true})});
            var Q75;
            Q75=makeQuery(id+"F4.boolean.opBoolean","COPY",EDGE,{"derivedFrom":makeQuery(id+"F4.opExtrude","CAP_EDGE",EDGE,{"disambiguationData":[OSD([sQuery(id+"F0.wireOp",EDGE,"E6.1.1.2")])],"isStart":true})});
            var Q76;
            Q76=makeQuery(id+"F4.boolean.opBoolean","COPY",EDGE,{"derivedFrom":makeQuery(id+"F4.opExtrude","CAP_EDGE",EDGE,{"disambiguationData":[OSD([sQuery(id+"F0.wireOp",EDGE,"E6.0.1.4")])],"isStart":true})});
            var Q77;
            Q77=makeQuery(id+"F4.boolean.opBoolean","COPY",EDGE,{"derivedFrom":makeQuery(id+"F4.opExtrude","CAP_EDGE",EDGE,{"disambiguationData":[OSD([sQuery(id+"F0.wireOp",EDGE,"E6.1.1.7")])],"isStart":true})});
            var Q78;
            Q78=makeQuery(id+"F4.boolean.opBoolean","COPY",EDGE,{"derivedFrom":makeQuery(id+"F4.opExtrude","CAP_EDGE",EDGE,{"disambiguationData":[OSD([sQuery(id+"F0.wireOp",EDGE,"E5.4")])],"isStart":true})});
            var Q79;
            Q79=makeQuery(id+"F3.boolean.opBoolean","COPY",EDGE,{"derivedFrom":makeQuery(id+"F3.opExtrude","CAP_EDGE",EDGE,{"disambiguationData":[OSD([sQuery(id+"F0.wireOp",EDGE,"E74.MirrorCS")])],"isStart":true})});
            var Q80;
            Q80=makeQuery(id+"F4.boolean.opBoolean","COPY",EDGE,{"derivedFrom":makeQuery(id+"F4.opExtrude","CAP_EDGE",EDGE,{"disambiguationData":[OSD([sQuery(id+"F0.wireOp",EDGE,"E5.0")])],"isStart":true})});
            var Q81;
            Q81=makeQuery(id+"F4.boolean.opBoolean","COPY",EDGE,{"derivedFrom":makeQuery(id+"F4.opExtrude","CAP_EDGE",EDGE,{"disambiguationData":[OSD([sQuery(id+"F0.wireOp",EDGE,"E5.2")])],"isStart":true})});
            var Q82;
            Q82=makeQuery(id+"F3.boolean.opBoolean","COPY",EDGE,{"derivedFrom":makeQuery(id+"F3.opExtrude","CAP_EDGE",EDGE,{"disambiguationData":[OSD([sQuery(id+"F0.wireOp",EDGE,"E70.MirrorCS")])],"isStart":true})});
            var Q83;
            Q83=makeQuery(id+"F3.boolean.opBoolean","COPY",EDGE,{"derivedFrom":makeQuery(id+"F3.opExtrude","CAP_EDGE",EDGE,{"disambiguationData":[OSD([sQuery(id+"F0.wireOp",EDGE,"E72.MirrorCS")])],"isStart":true})});
            var Q84;
            Q84=makeQuery(id+"F3.boolean.opBoolean","COPY",EDGE,{"derivedFrom":makeQuery(id+"F3.opExtrude","CAP_EDGE",EDGE,{"disambiguationData":[OSD([sQuery(id+"F0.wireOp",EDGE,"E64.MirrorCS")])],"isStart":true})});
            var Q85;
            Q85=makeQuery(id+"F4.boolean.opBoolean","COPY",EDGE,{"derivedFrom":makeQuery(id+"F4.opExtrude","CAP_EDGE",EDGE,{"disambiguationData":[OSD([sQuery(id+"F0.wireOp",EDGE,"E6.1.0.4")])],"isStart":true})});
            var Q86;
            Q86=makeQuery(id+"F3.boolean.opBoolean","COPY",EDGE,{"derivedFrom":makeQuery(id+"F3.opExtrude","CAP_EDGE",EDGE,{"disambiguationData":[OSD([sQuery(id+"F0.wireOp",EDGE,"E71.MirrorCS")])],"isStart":true})});
            var Q87;
            Q87=makeQuery(id+"F4.boolean.opBoolean","COPY",EDGE,{"derivedFrom":makeQuery(id+"F4.opExtrude","CAP_EDGE",EDGE,{"disambiguationData":[OSD([sQuery(id+"F0.wireOp",EDGE,"E6.1.0.5")])],"isStart":true})});
            var Q88;
            Q88=makeQuery(id+"F4.boolean.opBoolean","COPY",EDGE,{"derivedFrom":makeQuery(id+"F4.opExtrude","CAP_EDGE",EDGE,{"disambiguationData":[OSD([sQuery(id+"F0.wireOp",EDGE,"E6.1.0.1")])],"isStart":true})});
            var Q89;
            Q89=makeQuery(id+"F4.boolean.opBoolean","COPY",EDGE,{"derivedFrom":makeQuery(id+"F4.opExtrude","CAP_EDGE",EDGE,{"disambiguationData":[OSD([sQuery(id+"F0.wireOp",EDGE,"E5.5")])],"isStart":true})});
            var Q90;
            Q90=makeQuery(id+"F2.opExtrude","SWEPT_FACE",FACE,{"disambiguationData":[OSD([sQuery(id+"F1.wireOp",EDGE,"E92.0")])]});
            var Q91;
            Q91=makeQuery(id+"F3.boolean.opBoolean","COPY",EDGE,{"derivedFrom":makeQuery(id+"F3.opExtrude","CAP_EDGE",EDGE,{"disambiguationData":[OSD([sQuery(id+"F0.wireOp",EDGE,"E84.MirrorCS")])],"isStart":true})});
            var Q92;
            Q92=makeQuery(id+"F4.boolean.opBoolean","COPY",EDGE,{"derivedFrom":makeQuery(id+"F4.opExtrude","CAP_EDGE",EDGE,{"disambiguationData":[OSD([sQuery(id+"F0.wireOp",EDGE,"E6.3.1.5")])],"isStart":true})});
            var Q93;
            Q93=makeQuery(id+"F4.boolean.opBoolean","COPY",EDGE,{"derivedFrom":makeQuery(id+"F4.opExtrude","CAP_EDGE",EDGE,{"disambiguationData":[OSD([sQuery(id+"F0.wireOp",EDGE,"E6.2.1.2")])],"isStart":true})});
            var Q94;
            Q94=makeQuery(id+"F4.boolean.opBoolean","COPY",EDGE,{"derivedFrom":makeQuery(id+"F4.opExtrude","CAP_EDGE",EDGE,{"disambiguationData":[OSD([sQuery(id+"F0.wireOp",EDGE,"E6.3.0.0")])],"isStart":true})});
            var Q95;
            Q95=makeQuery(id+"F3.boolean.opBoolean","COPY",EDGE,{"derivedFrom":makeQuery(id+"F3.opExtrude","CAP_EDGE",EDGE,{"disambiguationData":[OSD([sQuery(id+"F0.wireOp",EDGE,"E82.MirrorCS")])],"isStart":true})});
            var Q96;
            Q96=makeQuery(id+"F4.boolean.opBoolean","COPY",EDGE,{"derivedFrom":makeQuery(id+"F4.opExtrude","CAP_EDGE",EDGE,{"disambiguationData":[OSD([sQuery(id+"F0.wireOp",EDGE,"E6.2.0.2")])],"isStart":true})});
            var Q97;
            Q97=makeQuery(id+"F4.boolean.opBoolean","COPY",EDGE,{"derivedFrom":makeQuery(id+"F4.opExtrude","CAP_EDGE",EDGE,{"disambiguationData":[OSD([sQuery(id+"F0.wireOp",EDGE,"E6.2.0.5")])],"isStart":true})});
            var Q98;
            Q98=makeQuery(id+"F3.boolean.opBoolean","COPY",EDGE,{"derivedFrom":makeQuery(id+"F3.opExtrude","CAP_EDGE",EDGE,{"disambiguationData":[OSD([sQuery(id+"F0.wireOp",EDGE,"E80.MirrorCS")])],"isStart":true})});
            var Q99;
            Q99=makeQuery(id+"F4.boolean.opBoolean","COPY",EDGE,{"derivedFrom":makeQuery(id+"F4.opExtrude","CAP_EDGE",EDGE,{"disambiguationData":[OSD([sQuery(id+"F0.wireOp",EDGE,"E6.2.1.7")])],"isStart":true})});
            var Q100;
            Q100=makeQuery(id+"F3.boolean.opBoolean","COPY",EDGE,{"derivedFrom":makeQuery(id+"F3.opExtrude","CAP_EDGE",EDGE,{"disambiguationData":[OSD([sQuery(id+"F0.wireOp",EDGE,"E77.MirrorCS")])],"isStart":true})});
            var Q101;
            Q101=makeQuery(id+"F4.boolean.opBoolean","COPY",EDGE,{"derivedFrom":makeQuery(id+"F4.opExtrude","CAP_EDGE",EDGE,{"disambiguationData":[OSD([sQuery(id+"F0.wireOp",EDGE,"E6.2.0.0")])],"isStart":true})});
            var Q102;
            Q102=makeQuery(id+"F4.boolean.opBoolean","COPY",EDGE,{"derivedFrom":makeQuery(id+"F4.opExtrude","CAP_EDGE",EDGE,{"disambiguationData":[OSD([sQuery(id+"F0.wireOp",EDGE,"E6.3.1.0")])],"isStart":true})});
            var Q103;
            Q103=makeQuery(id+"F3.boolean.opBoolean","COPY",EDGE,{"derivedFrom":makeQuery(id+"F3.opExtrude","CAP_EDGE",EDGE,{"disambiguationData":[OSD([sQuery(id+"F0.wireOp",EDGE,"E78.MirrorCS")])],"isStart":true})});
            var Q104;
            Q104=makeQuery(id+"F4.boolean.opBoolean","COPY",EDGE,{"derivedFrom":makeQuery(id+"F4.opExtrude","CAP_EDGE",EDGE,{"disambiguationData":[OSD([sQuery(id+"F0.wireOp",EDGE,"E6.2.1.0")])],"isStart":true})});
            var Q105;
            Q105=makeQuery(id+"F4.boolean.opBoolean","COPY",EDGE,{"derivedFrom":makeQuery(id+"F4.opExtrude","CAP_EDGE",EDGE,{"disambiguationData":[OSD([sQuery(id+"F0.wireOp",EDGE,"E6.3.0.1")])],"isStart":true})});
            var Q106;
            Q106=makeQuery(id+"F4.boolean.opBoolean","COPY",EDGE,{"derivedFrom":makeQuery(id+"F4.opExtrude","CAP_EDGE",EDGE,{"disambiguationData":[OSD([sQuery(id+"F0.wireOp",EDGE,"E6.2.0.1")])],"isStart":true})});
            var Q107;
            Q107=makeQuery(id+"F4.boolean.opBoolean","COPY",EDGE,{"derivedFrom":makeQuery(id+"F4.opExtrude","CAP_EDGE",EDGE,{"disambiguationData":[OSD([sQuery(id+"F0.wireOp",EDGE,"E6.2.1.5")])],"isStart":true})});
            var Q108;
            Q108=makeQuery(id+"F3.boolean.opBoolean","COPY",EDGE,{"derivedFrom":makeQuery(id+"F3.opExtrude","CAP_EDGE",EDGE,{"disambiguationData":[OSD([sQuery(id+"F0.wireOp",EDGE,"E81.MirrorCS")])],"isStart":true})});
            var Q109;
            Q109=makeQuery(id+"F4.boolean.opBoolean","COPY",EDGE,{"derivedFrom":makeQuery(id+"F4.opExtrude","CAP_EDGE",EDGE,{"disambiguationData":[OSD([sQuery(id+"F0.wireOp",EDGE,"E6.3.0.5")])],"isStart":true})});
            var Q110;
            Q110=makeQuery(id+"F3.boolean.opBoolean","COPY",EDGE,{"derivedFrom":makeQuery(id+"F3.opExtrude","CAP_EDGE",EDGE,{"disambiguationData":[OSD([sQuery(id+"F0.wireOp",EDGE,"E83.MirrorCS")])],"isStart":true})});
            var Q111;
            Q111=makeQuery(id+"F4.boolean.opBoolean","COPY",EDGE,{"derivedFrom":makeQuery(id+"F4.opExtrude","CAP_EDGE",EDGE,{"disambiguationData":[OSD([sQuery(id+"F0.wireOp",EDGE,"E6.3.0.4")])],"isStart":true})});
            var Q112;
            Q112=makeQuery(id+"F4.boolean.opBoolean","COPY",EDGE,{"derivedFrom":makeQuery(id+"F4.opExtrude","CAP_EDGE",EDGE,{"disambiguationData":[OSD([sQuery(id+"F0.wireOp",EDGE,"E6.2.0.4")])],"isStart":true})});
            var Q113;
            Q113=makeQuery(id+"F4.boolean.opBoolean","COPY",EDGE,{"derivedFrom":makeQuery(id+"F4.opExtrude","CAP_EDGE",EDGE,{"disambiguationData":[OSD([sQuery(id+"F0.wireOp",EDGE,"E6.3.0.2")])],"isStart":true})});
            var Q114;
            Q114=makeQuery(id+"F4.boolean.opBoolean","COPY",EDGE,{"derivedFrom":makeQuery(id+"F4.opExtrude","CAP_EDGE",EDGE,{"disambiguationData":[OSD([sQuery(id+"F0.wireOp",EDGE,"E6.2.1.4")])],"isStart":true})});
            var Q115;
            Q115=makeQuery(id+"F4.boolean.opBoolean","COPY",EDGE,{"derivedFrom":makeQuery(id+"F4.opExtrude","CAP_EDGE",EDGE,{"disambiguationData":[OSD([sQuery(id+"F0.wireOp",EDGE,"E6.3.1.2")])],"isStart":true})});
            var Q116;
            Q116=makeQuery(id+"F3.boolean.opBoolean","COPY",EDGE,{"derivedFrom":makeQuery(id+"F3.opExtrude","CAP_EDGE",EDGE,{"disambiguationData":[OSD([sQuery(id+"F0.wireOp",EDGE,"E85.MirrorCS")])],"isStart":true})});
            var Q117;
            Q117=makeQuery(id+"F3.boolean.opBoolean","COPY",EDGE,{"derivedFrom":makeQuery(id+"F3.opExtrude","CAP_EDGE",EDGE,{"disambiguationData":[OSD([sQuery(id+"F0.wireOp",EDGE,"E79.MirrorCS")])],"isStart":true})});
            var Q118;
            Q118=makeQuery(id+"F3.boolean.opBoolean","COPY",EDGE,{"derivedFrom":makeQuery(id+"F3.opExtrude","CAP_EDGE",EDGE,{"disambiguationData":[OSD([sQuery(id+"F0.wireOp",EDGE,"E75.MirrorCS")])],"isStart":true})});
            var Q119;
            Q119=makeQuery(id+"F4.boolean.opBoolean","COPY",EDGE,{"derivedFrom":makeQuery(id+"F4.opExtrude","CAP_EDGE",EDGE,{"disambiguationData":[OSD([sQuery(id+"F0.wireOp",EDGE,"E6.3.1.1")])],"isStart":true})});
            var Q120;
            Q120=makeQuery(id+"F3.boolean.opBoolean","COPY",EDGE,{"derivedFrom":makeQuery(id+"F3.opExtrude","CAP_EDGE",EDGE,{"disambiguationData":[OSD([sQuery(id+"F0.wireOp",EDGE,"E76.MirrorCS")])],"isStart":true})});
            var Q121;
            Q121=makeQuery(id+"F4.boolean.opBoolean","COPY",EDGE,{"derivedFrom":makeQuery(id+"F4.opExtrude","CAP_EDGE",EDGE,{"disambiguationData":[OSD([sQuery(id+"F0.wireOp",EDGE,"E6.3.0.7")])],"isStart":true})});
            var Q122;
            Q122=makeQuery(id+"F4.boolean.opBoolean","COPY",EDGE,{"derivedFrom":makeQuery(id+"F4.opExtrude","CAP_EDGE",EDGE,{"disambiguationData":[OSD([sQuery(id+"F0.wireOp",EDGE,"E6.3.1.7")])],"isStart":true})});
            var Q123;
            Q123=makeQuery(id+"F4.boolean.opBoolean","COPY",EDGE,{"derivedFrom":makeQuery(id+"F4.opExtrude","CAP_EDGE",EDGE,{"disambiguationData":[OSD([sQuery(id+"F0.wireOp",EDGE,"E6.2.1.1")])],"isStart":true})});
            var Q124;
            Q124=makeQuery(id+"F4.boolean.opBoolean","COPY",EDGE,{"derivedFrom":makeQuery(id+"F4.opExtrude","CAP_EDGE",EDGE,{"disambiguationData":[OSD([sQuery(id+"F0.wireOp",EDGE,"E6.2.0.7")])],"isStart":true})});
            var Q125;
            Q125=makeQuery(id+"F4.boolean.opBoolean","COPY",EDGE,{"derivedFrom":makeQuery(id+"F4.opExtrude","CAP_EDGE",EDGE,{"disambiguationData":[OSD([sQuery(id+"F0.wireOp",EDGE,"E6.3.1.4")])],"isStart":true})});
            var Q126;
            Q126=makeQuery(id+"F3.boolean.opBoolean","COPY",EDGE,{"derivedFrom":makeQuery(id+"F3.opExtrude","CAP_EDGE",EDGE,{"disambiguationData":[OSD([sQuery(id+"F0.wireOp",EDGE,"E86.MirrorCS")])],"isStart":true})});
            fillet(context, id + "F6", {"entities" : qUnion([Q0, Q1, Q2, Q3, Q4, Q5, Q6, Q7, Q8, Q9, Q10, Q11, Q12, Q13, Q14, Q15, Q16, Q17, Q18, Q19, Q20, Q21, Q22, Q23, Q24, Q25, Q26, Q27, Q28, Q29, Q30, Q31, Q32, Q33, Q34, Q35, Q36, Q37, Q38, Q39, Q40, Q41, Q42, Q43, Q44, Q45, Q46, Q47, Q48, Q49, Q50, Q51, Q52, Q53, Q54, Q55, Q56, Q57, Q58, Q59, Q60, Q61, Q62, Q63, Q64, Q65, Q66, Q67, Q68, Q69, Q70, Q71, Q72, Q73, Q74, Q75, Q76, Q77, Q78, Q79, Q80, Q81, Q82, Q83, Q84, Q85, Q86, Q87, Q88, Q89, Q90, Q91, Q92, Q93, Q94, Q95, Q96, Q97, Q98, Q99, Q100, Q101, Q102, Q103, Q104, Q105, Q106, Q107, Q108, Q109, Q110, Q111, Q112, Q113, Q114, Q115, Q116, Q117, Q118, Q119, Q120, Q121, Q122, Q123, Q124, Q125, Q126]), "radius" : .75 * mm, "tangentPropagation" : true, "allowEdgeOverflow" : false});
        }
    });
